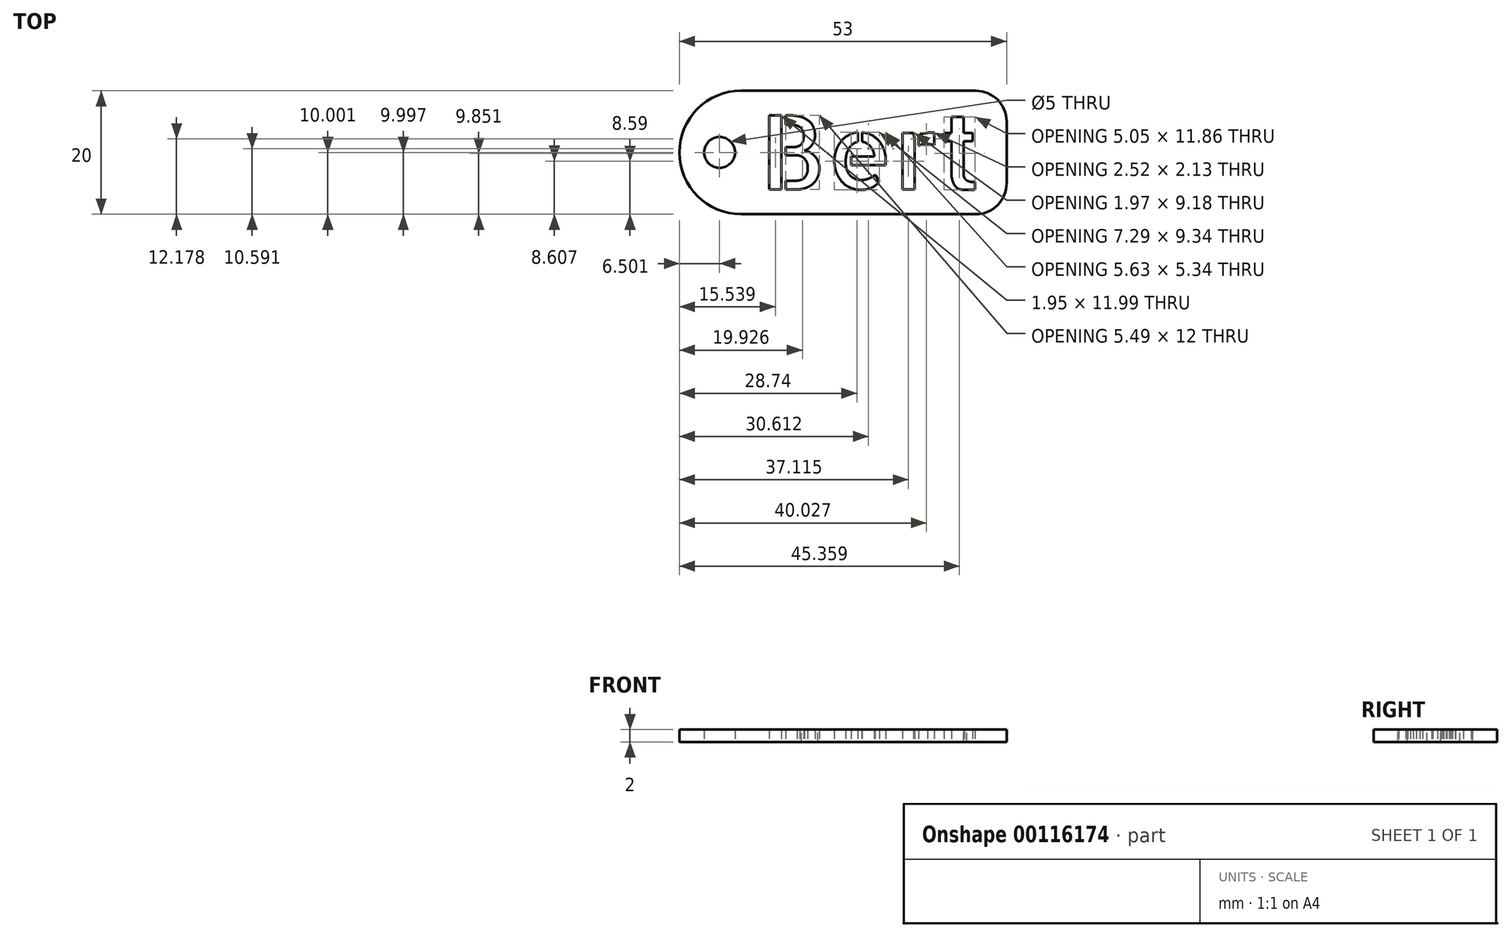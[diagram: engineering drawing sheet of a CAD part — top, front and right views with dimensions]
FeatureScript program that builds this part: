
annotation { "Feature Type Name" : "Feature", "Feature Type Description" : "" }
export const myFeature = defineFeature(function(context is Context, id is Id, definition is map)
    precondition{}
    {
        {
            var Q0;
            Q0=qCreatedBy(makeId("Top.planeOp"),FACE);
            var sketch = newSketch(context, id + "F0", { "sketchPlane" : qUnion([Q0])});
            skText(sketch, "E0", { "text": "Bert", "fontName": "AllertaStencil-Regular.ttf"});
            skLineSegment(sketch, "E1.bottom", {"start": v(19.91, 0.93) * mm, "end": v(62.9, 0.93) * mm});
            skLineSegment(sketch, "E1.top", {"start": v(19.91, -19.07) * mm, "end": v(62.9, -19.07) * mm});
            skLineSegment(sketch, "E1.left", {"start": v(19.91, 0.93) * mm, "end": v(19.91, -19.07) * mm});
            skLineSegment(sketch, "E1.right", {"start": v(62.9, 0.93) * mm, "end": v(62.9, -19.07) * mm});
            skArc(sketch, "E2", {"start": v(19.91, 0.93) * mm, "mid": v(9.91, -9.07) * mm, "end": v(19.91, -19.07) * mm});
            skLineSegment(sketch, "E3", {"start": v(19.91, -9.07) * mm, "end": v(9.91, -9.07) * mm, "construction": true});
            skCircle(sketch, "E4", {"center": v(16.41, -9.07) * mm, "radius": 2.5 * mm});
            const initialGuessF0  = {"E0": [0.02291, -0.01507, 1, 0, 0.012]};
            skSetInitialGuess(sketch, initialGuessF0);
            skSolve(sketch);
        }
        {
            var Q0;
            Q0=makeQuery(id+"F0.imprint","IMPRINT",FACE,{"disambiguationData":[TD([[makeQuery(id+"F0.imprint","IMPRINT",EDGE,{"derivedFrom":sQuery(id+"F0.wireOp",EDGE,"E1.left")}),-1.0]])]});
            var Q1;
            Q1=makeQuery(id+"F0.imprint","IMPRINT",FACE,{"disambiguationData":[TD([[makeQuery(id+"F0.imprint","IMPRINT",EDGE,{"derivedFrom":sQuery(id+"F0.wireOp",EDGE,"E0.sketch_text.stroke-0")}),1.0]])]});
            extrude(context, id + "F1", {"entities" : qUnion([Q0, Q1]), "depth" : 2 * mm});
        }
        {
            var Q0;
            Q0=makeQuery(id+"F1.opExtrude","SWEPT_EDGE",EDGE,{"disambiguationData":[OSD([sQuery(id+"F0.wireOp",EDGE,"E1.top"),sQuery(id+"F0.wireOp",EDGE,"E1.right")])]});
            var Q1;
            Q1=makeQuery(id+"F1.opExtrude","SWEPT_EDGE",EDGE,{"disambiguationData":[OSD([sQuery(id+"F0.wireOp",EDGE,"E1.bottom"),sQuery(id+"F0.wireOp",EDGE,"E1.right")])]});
            fillet(context, id + "F2", {"entities" : qUnion([Q0, Q1]), "radius" : 5 * mm, "tangentPropagation" : true, "allowEdgeOverflow" : false});
        }
    });
